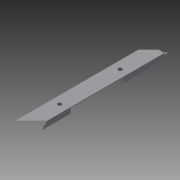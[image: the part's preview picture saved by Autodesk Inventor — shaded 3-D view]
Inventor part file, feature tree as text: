
AUTODESK INVENTOR PART (.ipt)
format: ipt  version: 2015 (Build 190159000, 159)  size: 177,152 bytes
history: native  units: in
note: dims shown in document units (in); Inventor stores cm internally (conversion verified against a paired STEP export)
features: sketch x7, extrude x6, projected_geometry x5, reference x2, chamfer x1, fillet x1
ambient origin geometry x8: Origin, YZ Plane, XZ Plane, XY Plane, X Axis, Y Axis, Z Axis, Center Point
bodies: Solid1 (feature_tree)
feature tree (22):
  extrude  "Extrusion1"  Depth=1.0in
  extrude  "Extrusion2"  Depth=0.25in
  extrude  "Extrusion3"  Depth=4.8in TaperAngle=0.0deg
  extrude  "Extrusion4"  Depth=0.1in TaperAngle=0.0deg
  chamfer  "Chamfer1"  Distance=0.0625in
  fillet  "Fillet1"  Radius=0.375in
  sketch  "Sketch7"  dims[d19=0.4375in d20=0.3in d21=0.0in]
  extrude  "Extrusion6"  Depth=0.3in TaperAngle=0.0deg
  extrude  "Extrusion5"  Depth=0.624in
  sketch  "Sketch1"  dims[d0=1.0in d1=0.25in]
  sketch  "Sketch2"  dims[d2=9.3625in d3=0.0in d6=0.25in]
  projected_geometry  "Projected Loop1"
  sketch  "Sketch3"  dims[d7=0.25in d8=4.8in d9=0.0in]
  reference  "Reference1"
  reference  "Reference2"
  projected_geometry  "Projected Loop2"
  sketch  "Sketch5"  dims[d10=3.8in d11=0.1in d12=0.0in d13=0.0625in d14=0.0in]
  projected_geometry  "Projected Loop4"
  sketch  "Sketch6"  dims[d15=0.25in d16=0.9375in d17=45.0deg d18=0.375in]
  projected_geometry  "Projected Loop5"
  sketch  "Sketch8"  dims[d22=0.6562in d23=0.0in d24=0.624in]
  projected_geometry  "Projected Loop6"
